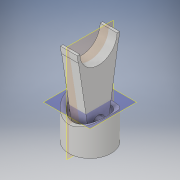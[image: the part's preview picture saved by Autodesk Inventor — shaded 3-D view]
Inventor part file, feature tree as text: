
AUTODESK INVENTOR PART (.ipt)
format: ipt  version: 2018 (Build 220112000, 112)  size: 168,448 bytes
history: native  units: in
note: dims shown in document units (in); Inventor stores cm internally (conversion verified against a paired STEP export)
features: sketch x8, extrude x7, projected_geometry x2, plane x1
ambient origin geometry x8: Origin, YZ Plane, XZ Plane, XY Plane, X Axis, Y Axis, Z Axis, Center Point
bodies: Solid1 (feature_tree)
feature tree (18):
  sketch  "Sketch1"  dims[d0=0.5in d1=0.3in d2=0.0in]
  extrude  "Extrusion1"  Depth=0.3in TaperAngle=0.0deg
  extrude  "Extrusion2"  Depth=0.1in
  plane  "Work Plane1"
  extrude  "Extrusion3"  [1 undecoded]
  extrude  "Extrusion4"  Depth=0.25in TaperAngle=0.0deg
  extrude  "Extrusion6"  Depth=0.1in
  extrude  "Extrusion5"  Depth=0.14in
  extrude  "Extrusion7"  Depth=0.25in
  sketch  "Sketch8"  dims[d22=0.0in d23=0.8in d26=0.5in d27=0.2in d28=0.0in d29=1.0in d30=0.0in d31=0.1in d32=0.0in]
  sketch  "Sketch2"  dims[d5=0.1in d6=0.35in]
  sketch  "Sketch3"  dims[d7=1.0in d8=0.0in d9=-0.3in]
  sketch  "Sketch4"  dims[d10=0.4in d11=0.25in d12=0.0in]
  sketch  "Sketch5"  dims[d13=0.1in d14=0.1in]
  sketch  "Sketch6"  dims[d15=0.45in d16=0.0in d17=0.14in]
  projected_geometry  "Projected Loop1"
  sketch  "Sketch7"  dims[d18=0.25in d21=0.44in]
  projected_geometry  "Projected Loop2"
note: 1 required parameter value undecoded (feature->parameter linkage not recoverable at this tier; creation-order binding heuristic only, values carry confidence <= 0.55)
